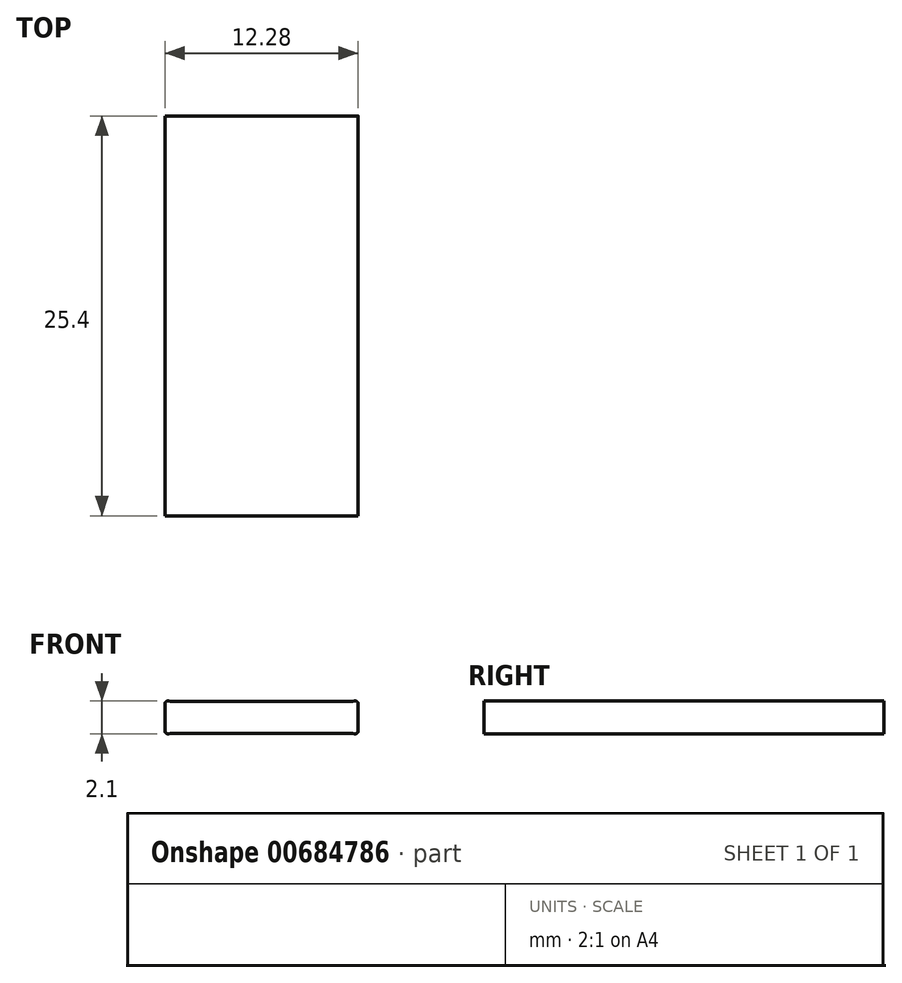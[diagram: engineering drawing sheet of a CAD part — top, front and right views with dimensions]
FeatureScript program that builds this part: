
annotation { "Feature Type Name" : "Feature", "Feature Type Description" : "" }
export const myFeature = defineFeature(function(context is Context, id is Id, definition is map)
    precondition{}
    {
        {
            var Q0;
            Q0=qCreatedBy(makeId("Front.planeOp"),FACE);
            var sketch = newSketch(context, id + "F0", { "sketchPlane" : qUnion([Q0])});
            skLineSegment(sketch, "E0.bottom", {"start": v(5.74, -1) * mm, "end": v(-5.74, -1) * mm});
            skLineSegment(sketch, "E0.top", {"start": v(5.74, 1) * mm, "end": v(-5.74, 1) * mm});
            skLineSegment(sketch, "E0.left", {"start": v(6.14, -0.84) * mm, "end": v(6.14, 0.84) * mm});
            skLineSegment(sketch, "E0.right", {"start": v(-6.14, -0.84) * mm, "end": v(-6.14, 0.84) * mm});
            skPoint(sketch, "E0.middle", {"position": v(0, 0) * mm});
            skArc(sketch, "E1", {"start": v(6.14, 0.84) * mm, "mid": v(6.07, 1) * mm, "end": v(5.9, 1.04) * mm});
            skArc(sketch, "E2", {"start": v(5.74, 1) * mm, "mid": v(5.75, 1) * mm, "end": v(5.76, 1.01) * mm});
            skLineSegment(sketch, "E3", {"start": v(5.9, 1.04) * mm, "end": v(5.76, 1.01) * mm});
            skPoint(sketch, "E4.orphan", {"position": v(6.14, 1) * mm});
            skArc(sketch, "E5.MirrorCS", {"start": v(-6.14, 0.84) * mm, "mid": v(-6.07, 1) * mm, "end": v(-5.9, 1.04) * mm});
            skLineSegment(sketch, "E6.MirrorCS", {"start": v(-5.9, 1.04) * mm, "end": v(-5.76, 1.01) * mm});
            skArc(sketch, "E7.MirrorCS", {"start": v(-5.74, 1) * mm, "mid": v(-5.75, 1) * mm, "end": v(-5.76, 1.01) * mm});
            skArc(sketch, "E8.MirrorCS", {"start": v(-6.14, -0.84) * mm, "mid": v(-6.07, -1) * mm, "end": v(-5.9, -1.04) * mm});
            skLineSegment(sketch, "E9.MirrorCS", {"start": v(-5.9, -1.04) * mm, "end": v(-5.76, -1.01) * mm});
            skArc(sketch, "E10.MirrorCS", {"start": v(-5.74, -1) * mm, "mid": v(-5.75, -1) * mm, "end": v(-5.76, -1.01) * mm});
            skArc(sketch, "E11.MirrorCS", {"start": v(6.14, -0.84) * mm, "mid": v(6.07, -1) * mm, "end": v(5.9, -1.04) * mm});
            skLineSegment(sketch, "E12.MirrorCS", {"start": v(5.9, -1.04) * mm, "end": v(5.76, -1.01) * mm});
            skArc(sketch, "E13.MirrorCS", {"start": v(5.74, -1) * mm, "mid": v(5.75, -1) * mm, "end": v(5.76, -1.01) * mm});
            skPoint(sketch, "E14.orphan", {"position": v(6.14, -1) * mm});
            skPoint(sketch, "E15.orphan", {"position": v(-6.14, 1) * mm});
            skPoint(sketch, "E16.orphan", {"position": v(-6.14, -1) * mm});
            skSolve(sketch);
        }
        {
            var Q0;
            Q0=makeQuery(id+"F0.imprint","IMPRINT",FACE,{"disambiguationData":[TD([[makeQuery(id+"F0.imprint","IMPRINT",EDGE,{"derivedFrom":sQuery(id+"F0.wireOp",EDGE,"E0.bottom")}),-1.0]])]});
            extrude(context, id + "F1", {"entities" : qUnion([Q0]), "endBound" : BoundingType.SYMMETRIC, "depth" : 25.4 * mm, "offsetDistance" : 25.4 * mm});
        }
    });
